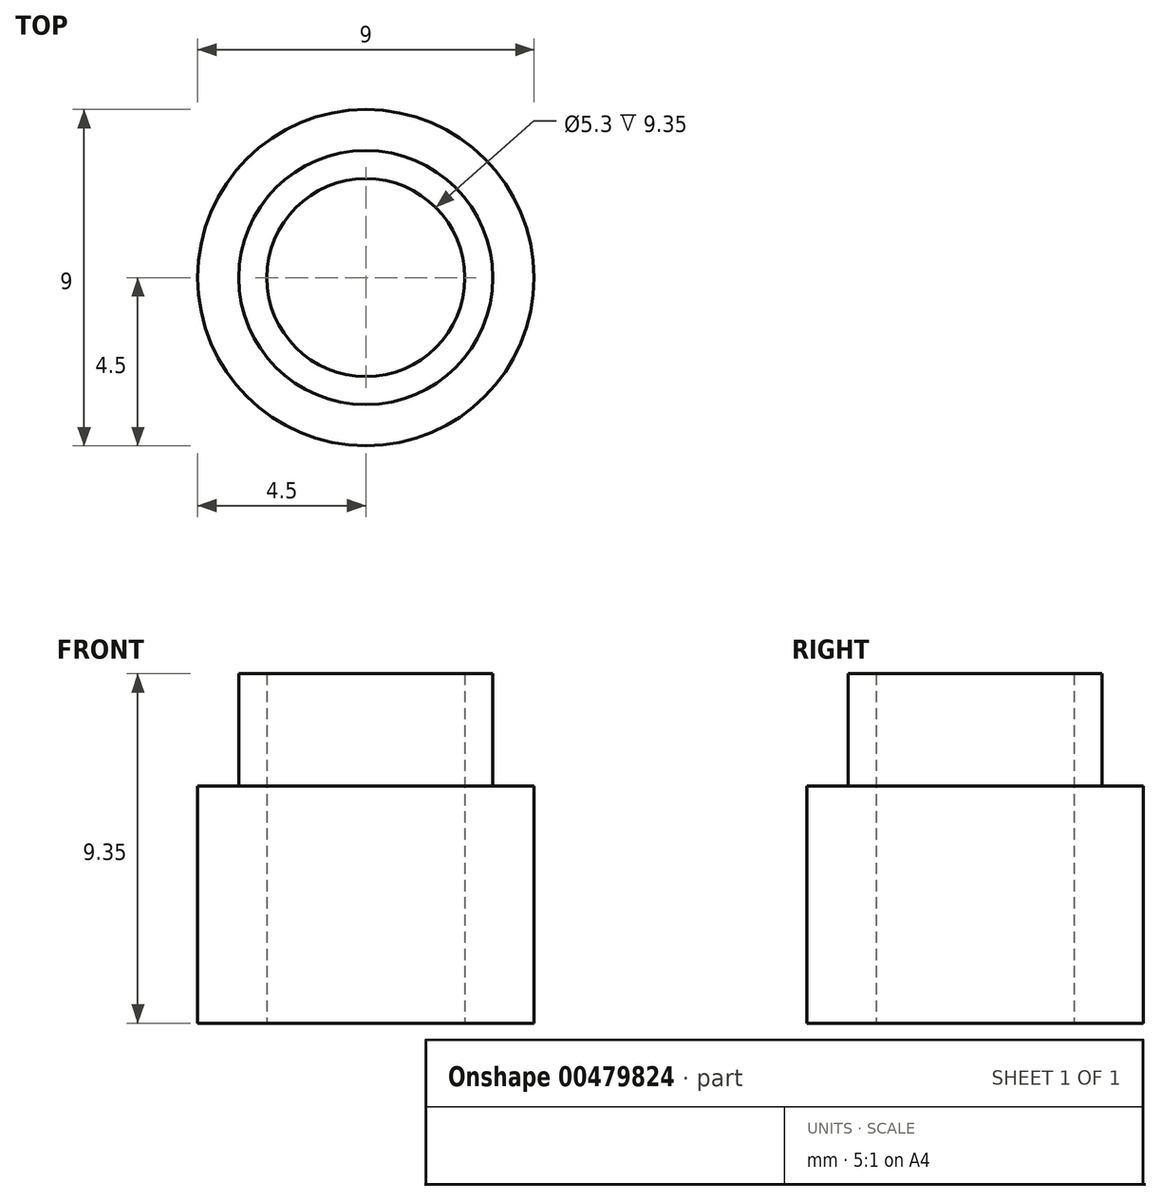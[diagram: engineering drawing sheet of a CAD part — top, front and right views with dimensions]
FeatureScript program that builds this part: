
annotation { "Feature Type Name" : "Feature", "Feature Type Description" : "" }
export const myFeature = defineFeature(function(context is Context, id is Id, definition is map)
    precondition{}
    {
        {
            var Q0;
            Q0=qCreatedBy(makeId("Top.planeOp"),FACE);
            var sketch = newSketch(context, id + "F0", { "sketchPlane" : qUnion([Q0])});
            skCircle(sketch, "E0", {"center": v(0, 0) * mm, "radius": 4.5 * mm});
            skSolve(sketch);
        }
        {
            var Q0;
            Q0=makeQuery(id+"F0.imprint","IMPRINT",FACE,{"disambiguationData":[TD([[makeQuery(id+"F0.imprint","IMPRINT",EDGE,{"derivedFrom":sQuery(id+"F0.wireOp",EDGE,"E0")}),1.0]])]});
            extrude(context, id + "F1", {"entities" : qUnion([Q0]), "depth" : 6.35 * mm});
        }
        {
            var Q0;
            Q0=makeQuery(id+"F1.opExtrude","CAP_FACE",FACE,{"disambiguationData":[OSD([sQuery(id+"F0.wireOp",EDGE,"E0")])],"isStart":false});
            var sketch = newSketch(context, id + "F2", { "sketchPlane" : qUnion([Q0])});
            skCircle(sketch, "E1", {"center": v(0, 0) * mm, "radius": 3.4 * mm});
            skSolve(sketch);
        }
        {
            var Q0;
            Q0 = qSketchRegion(id + "F2", true);
            extrude(context, id + "F3", {"entities" : qUnion([Q0]), "operationType" : NewBodyOperationType.ADD, "depth" : 3 * mm});
        }
        {
            var Q0;
            Q0=sQuery(id+"F0.wireOp",VERTEX,"E0.center");
            var Q1;
            Q1=makeQuery(id+"F1.opExtrude","SWEPT_BODY",BODY,{"disambiguationData":[OSD([sQuery(id+"F0.wireOp",EDGE,"E0")])]});
            hole(context, id + "F4", {"style" : HoleStyle.SIMPLE, "endStyle" : HoleEndStyle.THROUGH, "oppositeDirection" : true, "holeDiameter" : 5.3 * mm, "tappedDepth" : 12 * mm, "tapClearance" : 3, "locations" : qUnion([Q0]), "scope" : qUnion([Q1])});
        }
    });
